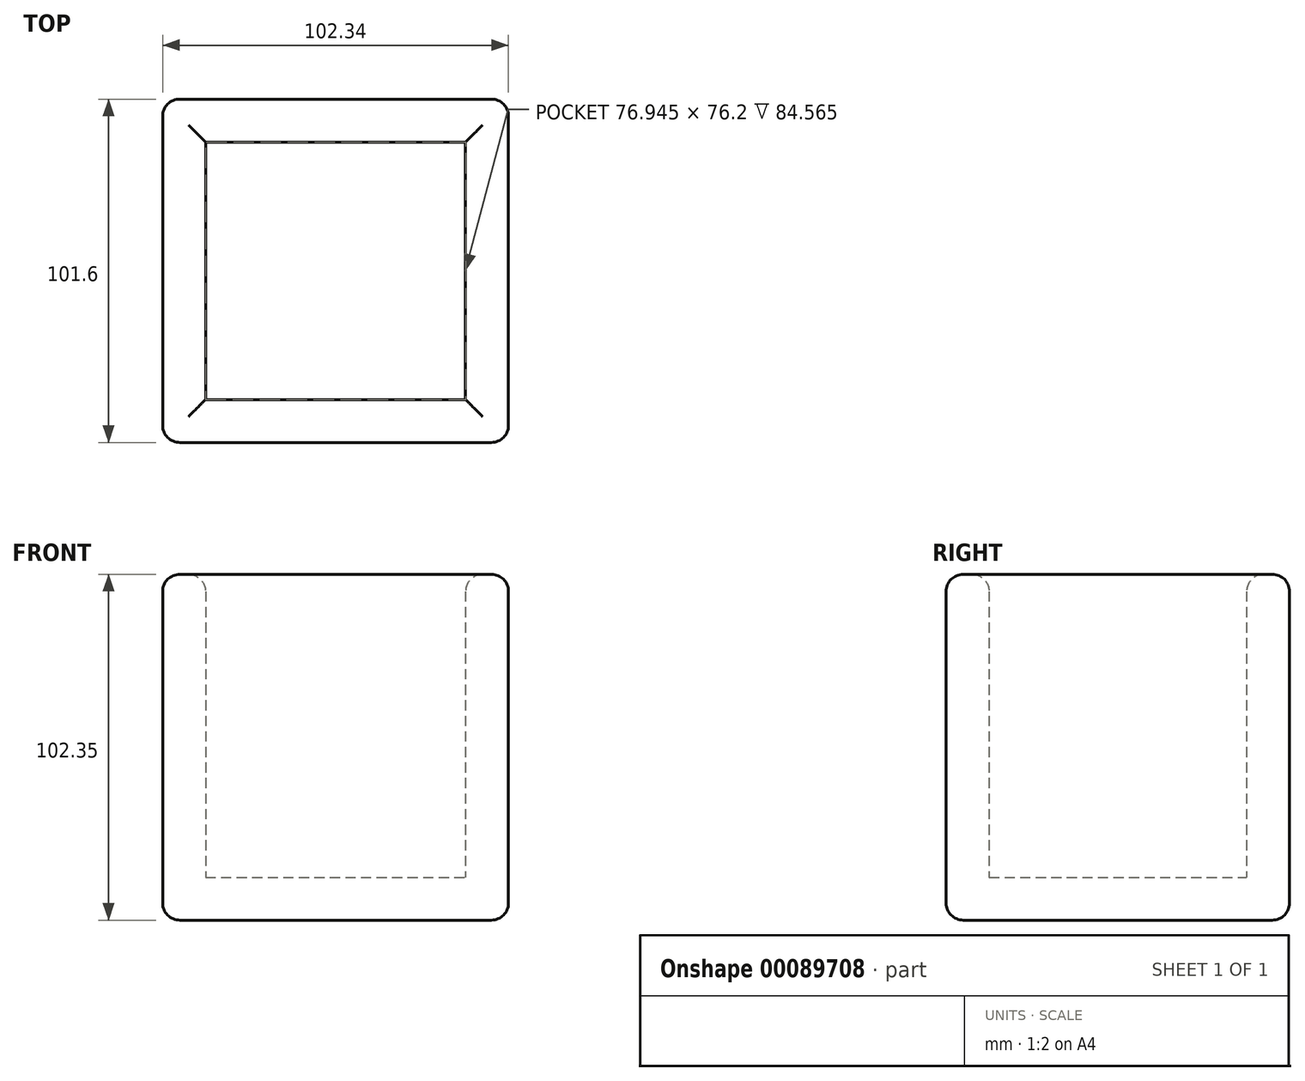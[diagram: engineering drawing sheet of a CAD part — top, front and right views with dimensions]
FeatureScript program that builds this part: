
annotation { "Feature Type Name" : "Feature", "Feature Type Description" : "" }
export const myFeature = defineFeature(function(context is Context, id is Id, definition is map)
    precondition{}
    {
        {
            var Q0;
            Q0=qCreatedBy(makeId("Front.planeOp"),FACE);
            var sketch = newSketch(context, id + "F0", { "sketchPlane" : qUnion([Q0])});
            skLineSegment(sketch, "E0.bottom", {"start": v(-60.5, 48.16) * mm, "end": v(41.84, 48.16) * mm});
            skLineSegment(sketch, "E0.top", {"start": v(-60.5, -54.19) * mm, "end": v(41.84, -54.19) * mm});
            skLineSegment(sketch, "E0.left", {"start": v(-60.5, 48.16) * mm, "end": v(-60.5, -54.19) * mm});
            skLineSegment(sketch, "E0.right", {"start": v(41.84, 48.16) * mm, "end": v(41.84, -54.19) * mm});
            skSolve(sketch);
        }
        {
            var Q0;
            Q0 = qSketchRegion(id + "F0", true);
            extrude(context, id + "F1", {"entities" : qUnion([Q0]), "depth" : 101.6 * mm});
        }
        {
            var Q0;
            Q0=makeQuery(id+"F1.opExtrude","SWEPT_FACE",FACE,{"disambiguationData":[OSD([sQuery(id+"F0.wireOp",EDGE,"E0.bottom")])]});
            shell(context, id + "F2", {"entities" : qUnion([Q0]), "thickness" : 12.7 * mm});
        }
        {
            var Q0;
            Q0=makeQuery(id+"F1.opExtrude","SWEPT_EDGE",EDGE,{"disambiguationData":[OSD([sQuery(id+"F0.wireOp",EDGE,"E0.bottom"),sQuery(id+"F0.wireOp",EDGE,"E0.right")])]});
            var Q1;
            Q1=makeQuery(id+"F1.opExtrude","CAP_EDGE",EDGE,{"disambiguationData":[OSD([sQuery(id+"F0.wireOp",EDGE,"E0.bottom")])],"isStart":false});
            var Q2;
            Q2=makeQuery(id+"F1.opExtrude","CAP_EDGE",EDGE,{"disambiguationData":[OSD([sQuery(id+"F0.wireOp",EDGE,"E0.right")])],"isStart":false});
            var Q3;
            Q3=makeQuery(id+"F1.opExtrude","SWEPT_EDGE",EDGE,{"disambiguationData":[OSD([sQuery(id+"F0.wireOp",EDGE,"E0.top"),sQuery(id+"F0.wireOp",EDGE,"E0.right")])]});
            var Q4;
            Q4=makeQuery(id+"F1.opExtrude","CAP_EDGE",EDGE,{"disambiguationData":[OSD([sQuery(id+"F0.wireOp",EDGE,"E0.top")])],"isStart":false});
            var Q5;
            {var subQ0=sQuery(id+"F0.wireOp",EDGE,"E0.bottom");Q5=makeQuery(id+"F2.opShell","OFFSET_EDGE",EDGE,{"disambiguationData":[OSD([subQ0]),TDD([makeQuery(id+"F1.opExtrude","CAP_EDGE",EDGE,{"disambiguationData":[OSD([subQ0])],"isStart":false})])]});}
            var Q6;
            Q6=makeQuery(id+"F1.opExtrude","SWEPT_FACE",FACE,{"disambiguationData":[OSD([sQuery(id+"F0.wireOp",EDGE,"E0.bottom")])]});
            var Q7;
            Q7=makeQuery(id+"F2.opShell","OFFSET_EDGE",EDGE,{"disambiguationData":[OSD([sQuery(id+"F0.wireOp",EDGE,"E0.bottom"),sQuery(id+"F0.wireOp",EDGE,"E0.right")])]});
            var Q8;
            {var subQ0=sQuery(id+"F0.wireOp",EDGE,"E0.bottom");Q8=makeQuery(id+"F2.opShell","OFFSET_EDGE",EDGE,{"disambiguationData":[OSD([subQ0]),TDD([makeQuery(id+"F1.opExtrude","CAP_EDGE",EDGE,{"disambiguationData":[OSD([subQ0])],"isStart":true})])]});}
            var Q9;
            Q9=makeQuery(id+"F2.opShell","OFFSET_EDGE",EDGE,{"disambiguationData":[OSD([sQuery(id+"F0.wireOp",EDGE,"E0.bottom"),sQuery(id+"F0.wireOp",EDGE,"E0.left")])]});
            var Q10;
            Q10=makeQuery(id+"F1.opExtrude","SWEPT_EDGE",EDGE,{"disambiguationData":[OSD([sQuery(id+"F0.wireOp",EDGE,"E0.bottom"),sQuery(id+"F0.wireOp",EDGE,"E0.left")])]});
            var Q11;
            Q11=makeQuery(id+"F1.opExtrude","CAP_EDGE",EDGE,{"disambiguationData":[OSD([sQuery(id+"F0.wireOp",EDGE,"E0.bottom")])],"isStart":true});
            fillet(context, id + "F3", {"entities" : qUnion([Q0, Q1, Q2, Q3, Q4, Q5, Q6, Q7, Q8, Q9, Q10, Q11]), "radius" : 5.08 * mm, "tangentPropagation" : true, "allowEdgeOverflow" : false});
        }
        {
            var Q0;
            Q0=makeQuery(id+"F1.opExtrude","CAP_EDGE",EDGE,{"disambiguationData":[OSD([sQuery(id+"F0.wireOp",EDGE,"E0.top")])],"isStart":true});
            var Q1;
            Q1=makeQuery(id+"F1.opExtrude","CAP_EDGE",EDGE,{"disambiguationData":[OSD([sQuery(id+"F0.wireOp",EDGE,"E0.left")])],"isStart":true});
            var Q2;
            Q2=makeQuery(id+"F1.opExtrude","SWEPT_EDGE",EDGE,{"disambiguationData":[OSD([sQuery(id+"F0.wireOp",EDGE,"E0.top"),sQuery(id+"F0.wireOp",EDGE,"E0.left")])]});
            fillet(context, id + "F4", {"entities" : qUnion([Q0, Q1, Q2]), "radius" : 5.08 * mm, "tangentPropagation" : true, "allowEdgeOverflow" : false});
        }
    });
